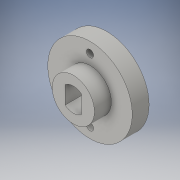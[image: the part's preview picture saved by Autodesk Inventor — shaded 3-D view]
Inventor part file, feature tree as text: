
AUTODESK INVENTOR PART (.ipt)
format: ipt  version: 2016 (Build 200138000, 138)  size: 122,368 bytes
history: native  units: in
note: dims shown in document units (in); Inventor stores cm internally (conversion verified against a paired STEP export)
features: extrude x2, sketch x2
ambient origin geometry x8: Origin, YZ Plane, XZ Plane, XY Plane, X Axis, Y Axis, Z Axis, Center Point
bodies: Solid1 (feature_tree)
feature tree (4):
  extrude  "Extrusion1"  Depth=0.2in
  extrude  "Extrusion2"  Depth=0.5in
  sketch  "Sketch1"  dims[d14=0.2in d15=0.0in d16=1.0in]
  sketch  "Sketch2"  dims[d17=0.085in d18=0.085in d19=0.085in d20=0.2in d21=0.0in d26=0.5in]
